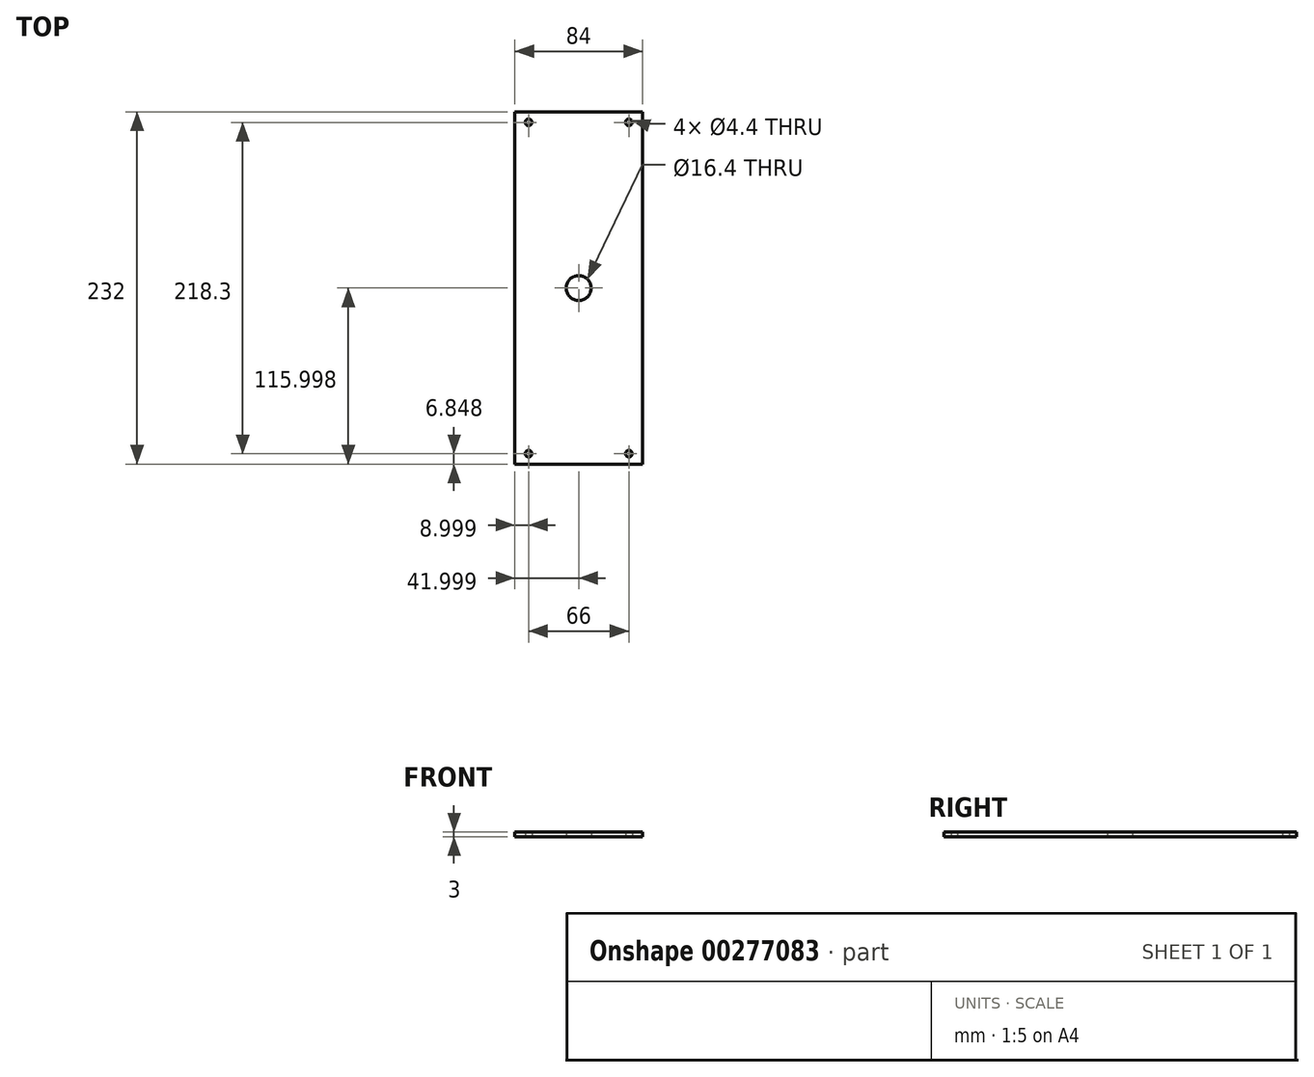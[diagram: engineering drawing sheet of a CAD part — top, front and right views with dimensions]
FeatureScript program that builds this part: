
annotation { "Feature Type Name" : "Feature", "Feature Type Description" : "" }
export const myFeature = defineFeature(function(context is Context, id is Id, definition is map)
    precondition{}
    {
        {
            var Q0;
            Q0=qCreatedBy(makeId("Top.planeOp"),FACE);
            var sketch = newSketch(context, id + "F0", { "sketchPlane" : qUnion([Q0])});
            skLineSegment(sketch, "E0.bottom", {"start": v(10.7, -38.44) * mm, "end": v(94.7, -38.44) * mm});
            skLineSegment(sketch, "E0.top", {"start": v(10.7, 193.56) * mm, "end": v(94.7, 193.56) * mm});
            skLineSegment(sketch, "E0.left", {"start": v(10.7, -38.44) * mm, "end": v(10.7, 193.56) * mm});
            skLineSegment(sketch, "E0.right", {"start": v(94.7, -38.44) * mm, "end": v(94.7, 193.56) * mm});
            skLineSegment(sketch, "E1", {"start": v(94.7, -31.6) * mm, "end": v(10.7, -31.6) * mm, "construction": true});
            skLineSegment(sketch, "E2", {"start": v(85.7, -38.44) * mm, "end": v(85.7, 193.56) * mm, "construction": true});
            skLineSegment(sketch, "E3", {"start": v(19.7, -38.44) * mm, "end": v(19.7, 193.56) * mm, "construction": true});
            skLineSegment(sketch, "E4", {"start": v(10.7, 186.7) * mm, "end": v(94.7, 186.7) * mm, "construction": true});
            skCircle(sketch, "E5", {"center": v(19.7, -31.6) * mm, "radius": 2.2 * mm});
            skCircle(sketch, "E6", {"center": v(85.7, -31.6) * mm, "radius": 2.2 * mm});
            skCircle(sketch, "E7", {"center": v(85.7, 186.7) * mm, "radius": 2.2 * mm});
            skCircle(sketch, "E8", {"center": v(19.7, 186.7) * mm, "radius": 2.2 * mm});
            skLineSegment(sketch, "E9", {"start": v(52.7, 193.56) * mm, "end": v(52.7, -38.44) * mm, "construction": true});
            skLineSegment(sketch, "E10", {"start": v(10.7, 77.56) * mm, "end": v(94.7, 77.56) * mm, "construction": true});
            skCircle(sketch, "E11", {"center": v(52.7, 77.56) * mm, "radius": 8.2 * mm});
            skSolve(sketch);
        }
        {
            var Q0;
            Q0 = qSketchRegion(id + "F0", true);
            extrude(context, id + "F1", {"entities" : qUnion([Q0]), "depth" : 3 * mm});
        }
    });
